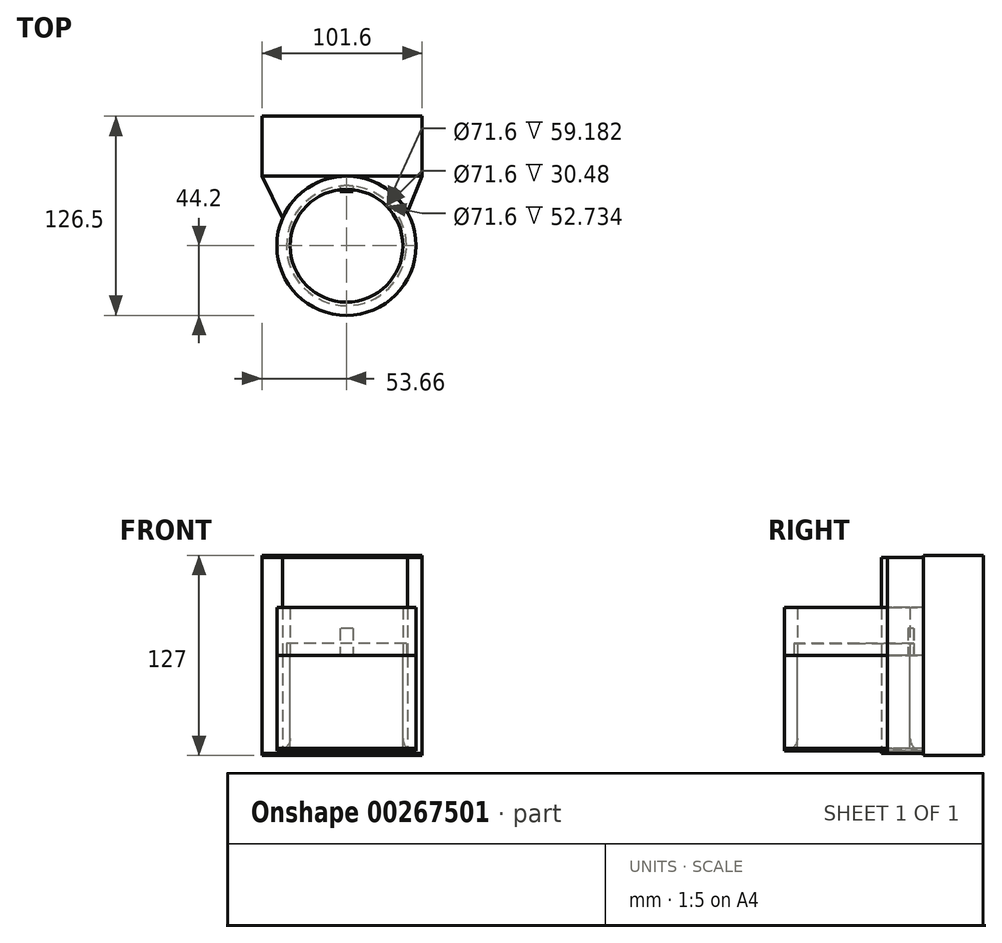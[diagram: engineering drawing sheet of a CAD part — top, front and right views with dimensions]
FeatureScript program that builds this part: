
annotation { "Feature Type Name" : "Feature", "Feature Type Description" : "" }
export const myFeature = defineFeature(function(context is Context, id is Id, definition is map)
    precondition{}
    {
        {
            var Q0;
            Q0=qCreatedBy(makeId("Top.planeOp"),FACE);
            var sketch = newSketch(context, id + "F0", { "sketchPlane" : qUnion([Q0])});
            skCircle(sketch, "E0", {"center": v(0, 0) * mm, "radius": 44.2 * mm});
            skPoint(sketch, "E1.middle", {"position": v(0, 44.2) * mm});
            skLineSegment(sketch, "E2", {"start": v(0, 44.2) * mm, "end": v(-53.66, 44.2) * mm});
            skLineSegment(sketch, "E3.bottom", {"start": v(-53.66, 44.2) * mm, "end": v(47.94, 44.2) * mm});
            skLineSegment(sketch, "E3.top", {"start": v(-53.66, 82.3) * mm, "end": v(47.94, 82.3) * mm});
            skLineSegment(sketch, "E3.left", {"start": v(-53.66, 44.2) * mm, "end": v(-53.66, 82.3) * mm});
            skLineSegment(sketch, "E3.right", {"start": v(47.94, 44.2) * mm, "end": v(47.94, 82.3) * mm});
            skLineSegment(sketch, "E4", {"start": v(-53.66, 44.2) * mm, "end": v(-40.53, 17.61) * mm});
            skLineSegment(sketch, "E5", {"start": v(47.94, 44.2) * mm, "end": v(38.72, 21.3) * mm});
            skCircle(sketch, "E6", {"center": v(0, 0) * mm, "radius": 35.8 * mm});
            skPoint(sketch, "E7.middle", {"position": v(0, 35.8) * mm});
            skSolve(sketch);
        }
        {
            var Q0;
            Q0=makeQuery(id+"F0.imprint","IMPRINT",FACE,{"disambiguationData":[TD([[makeQuery(id+"F0.imprint","IMPRINT",EDGE,{"derivedFrom":sQuery(id+"F0.wireOp",EDGE,"E3.top")}),-1.0]])]});
            extrude(context, id + "F1", {"entities" : qUnion([Q0]), "endBound" : BoundingType.SYMMETRIC, "depth" : 127 * mm});
        }
        {
            var Q0;
            {var subQ0=sQuery(id+"F0.wireOp",EDGE,"E4");Q0=makeQuery(id+"F0.imprint","IMPRINT",FACE,{"disambiguationData":[TD([[makeQuery(id+"F0.imprint","IMPRINT",EDGE,{"derivedFrom":subQ0}),1.0]])]});}
            var Q1;
            {var subQ0=sQuery(id+"F0.wireOp",EDGE,"E5");Q1=makeQuery(id+"F0.imprint","IMPRINT",FACE,{"disambiguationData":[TD([[makeQuery(id+"F0.imprint","IMPRINT",EDGE,{"derivedFrom":subQ0}),-1.0]])]});}
            extrude(context, id + "F2", {"entities" : qUnion([Q0, Q1]), "operationType" : NewBodyOperationType.ADD, "endBound" : BoundingType.SYMMETRIC, "depth" : 124.46 * mm});
        }
        {
            var Q0;
            Q0=makeQuery(id+"F0.imprint","IMPRINT",FACE,{"disambiguationData":[TD([[makeQuery(id+"F0.imprint","IMPRINT",EDGE,{"derivedFrom":sQuery(id+"F0.wireOp",EDGE,"E6")}),-1.0]])]});
            extrude(context, id + "F3", {"entities" : qUnion([Q0]), "operationType" : NewBodyOperationType.ADD, "oppositeDirection" : true, "depth" : 60.7 * mm});
        }
        {
            var Q0;
            Q0=makeQuery(id+"F3.opExtrude","CAP_EDGE",EDGE,{"disambiguationData":[OSD([sQuery(id+"F0.wireOp",EDGE,"E6")])],"isStart":false});
            fillet(context, id + "F4", {"entities" : qUnion([Q0]), "radius" : 7.97 * mm, "tangentPropagation" : true, "allowEdgeOverflow" : false});
        }
        {
            var Q0;
            Q0=qCreatedBy(makeId("Top.planeOp"),FACE);
            var sketch = newSketch(context, id + "F5", { "sketchPlane" : qUnion([Q0])});
            skCircle(sketch, "E8", {"center": v(0, 0) * mm, "radius": 38.1 * mm});
            skLineSegment(sketch, "E9.bottom", {"start": v(4.1, 41.93) * mm, "end": v(-4.1, 41.93) * mm});
            skLineSegment(sketch, "E9.top", {"start": v(4.1, 34.27) * mm, "end": v(-4.1, 34.27) * mm});
            skLineSegment(sketch, "E9.left", {"start": v(4.1, 41.93) * mm, "end": v(4.1, 34.27) * mm});
            skLineSegment(sketch, "E9.right", {"start": v(-4.1, 41.93) * mm, "end": v(-4.1, 34.27) * mm});
            skPoint(sketch, "E9.middle", {"position": v(0, 38.1) * mm});
            skSolve(sketch);
        }
        {
            var Q0;
            Q0=makeQuery(id+"F5.imprint","IMPRINT",FACE,{"disambiguationData":[TD([[makeQuery(id+"F5.imprint","IMPRINT",EDGE,{"derivedFrom":sQuery(id+"F5.wireOp",EDGE,"E8")}),1.0]])]});
            extrude(context, id + "F6", {"entities" : qUnion([Q0]), "depth" : 7.62 * mm});
        }
        {
            var Q0;
            {var subQ5=sQuery(id+"F5.wireOp",EDGE,"E9.top");Q0=makeQuery(id+"F5.imprint","IMPRINT",FACE,{"disambiguationData":[TD([[makeQuery(id+"F5.imprint","IMPRINT",EDGE,{"derivedFrom":subQ5}),-1.0]])]});}
            extrude(context, id + "F7", {"entities" : qUnion([Q0]), "depth" : 17.02 * mm});
        }
        {
            var Q0;
            {var subQ0=sQuery(id+"F0.wireOp",EDGE,"E7.left");var subQ5=sQuery(id+"F0.wireOp",EDGE,"E0");var subQ6=makeQuery(id+"F0.imprint","INTERSECT",VERTEX,{"derivedFrom":[subQ5,subQ0]});Q0=makeQuery(id+"F0.imprint","IMPRINT",FACE,{"disambiguationData":[TD([[makeQuery(id+"F0.imprint","IMPRINT",EDGE,{"disambiguationData":[TD([[subQ6,-1.0]])],"derivedFrom":subQ5}),1.0]])]});}
            extrude(context, id + "F8", {"entities" : qUnion([Q0]), "depth" : 30.48 * mm});
        }
        {
            var Q0;
            {var subQ5=sQuery(id+"F0.wireOp",EDGE,"E0");var subQ7=makeQuery(id+"F0.imprint","INTERSECT",VERTEX,{"derivedFrom":[subQ5,sQuery(id+"F0.wireOp",EDGE,"E5")]});Q0=makeQuery(id+"F0.imprint","IMPRINT",FACE,{"disambiguationData":[TD([[makeQuery(id+"F0.imprint","IMPRINT",EDGE,{"disambiguationData":[TD([[subQ7,-1.0]])],"derivedFrom":subQ5}),1.0]])]});}
            extrude(context, id + "F9", {"entities" : qUnion([Q0]), "oppositeDirection" : true, "depth" : 59.18 * mm});
        }
    });
